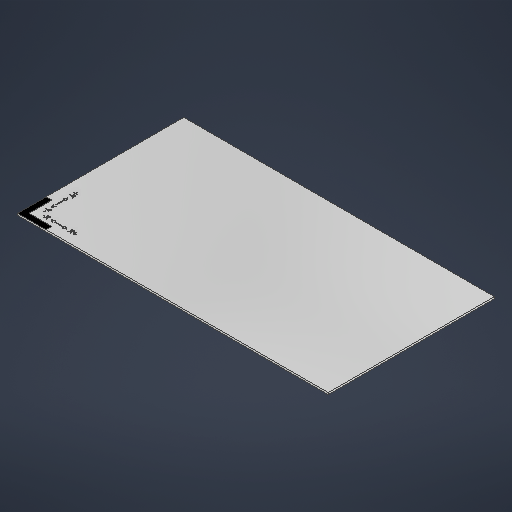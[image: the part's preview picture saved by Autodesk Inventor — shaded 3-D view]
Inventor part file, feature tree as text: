
AUTODESK INVENTOR PART (.ipt)
format: ipt  version: 2025.1 (Build 291241000, 241)  size: 346,624 bytes
history: native  units: mm
features: extrude x2, sketch x2
ambient origin geometry x8: Origin, YZ Plane, XZ Plane, XY Plane, X Axis, Y Axis, Z Axis, Center Point
bodies: Solid1 (feature_tree)
feature tree (4):
  extrude  "Extrusion1"  Depth=584.2mm
  extrude  "Extrusion2"  Depth=20.0mm
  sketch  "Sketch1"  dims[d0=1092.2mm d1=584.2mm]
  sketch  "Sketch2"  dims[d2=6.5mm d3=0.0mm d4=20.0mm d5=20.0mm d6=100.0mm d7=100.0mm d8=120.0mm d9=120.0mm d10=20.0mm d11=20.0mm d12=10.0mm d13=10.0mm d14=30.0mm d15=30.0mm d16=0.5mm d17=0.0mm]
